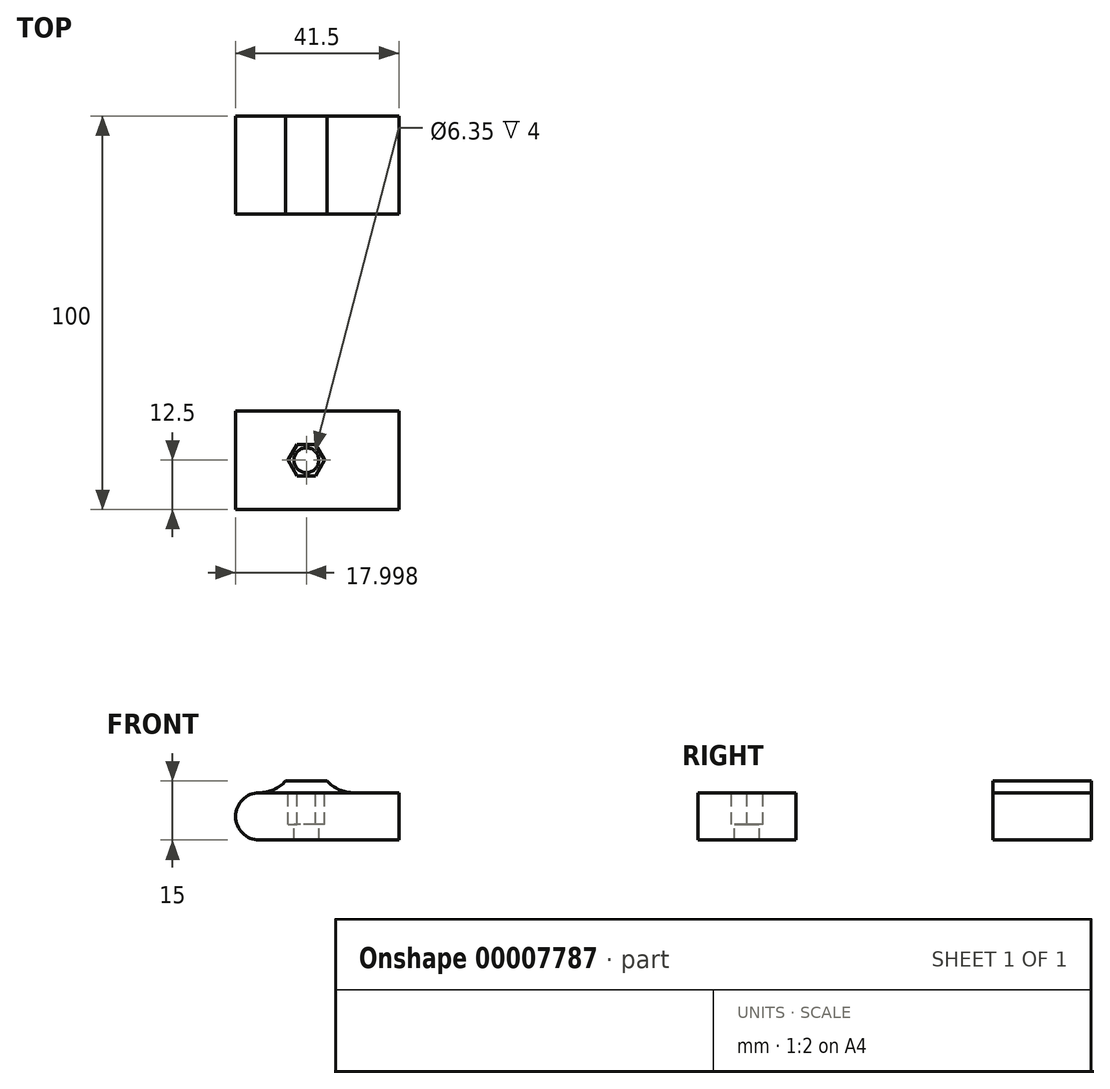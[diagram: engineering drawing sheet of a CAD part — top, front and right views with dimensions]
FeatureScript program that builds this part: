
annotation { "Feature Type Name" : "Feature", "Feature Type Description" : "" }
export const myFeature = defineFeature(function(context is Context, id is Id, definition is map)
    precondition{}
    {
        {
            var Q0;
            Q0=qCreatedBy(makeId("Front.planeOp"),FACE);
            var sketch = newSketch(context, id + "F0", { "sketchPlane" : qUnion([Q0])});
            skArc(sketch, "E0", {"start": v(-62.06, 7.13) * mm, "mid": v(-68.06, 1.13) * mm, "end": v(-62.06, -4.87) * mm});
            skLineSegment(sketch, "E1.rect.bottom", {"start": v(-44.77, 4.13) * mm, "end": v(-55.35, 4.13) * mm});
            skLineSegment(sketch, "E1.rect.top", {"start": v(-44.77, 10.13) * mm, "end": v(-55.35, 10.13) * mm});
            skLineSegment(sketch, "E1.rect.left", {"start": v(-44.77, 4.13) * mm, "end": v(-44.77, 10.13) * mm});
            skLineSegment(sketch, "E1.rect.right", {"start": v(-55.35, 4.13) * mm, "end": v(-55.35, 10.13) * mm});
            skPoint(sketch, "E1.rect.middle", {"position": v(-50.06, 7.13) * mm});
            skArc(sketch, "E2", {"start": v(-62.06, 7.13) * mm, "mid": v(-58.39, 7.92) * mm, "end": v(-55.35, 10.13) * mm});
            skLineSegment(sketch, "E3", {"start": v(-50.06, 7.13) * mm, "end": v(-50.06, 4.13) * mm, "construction": true});
            skArc(sketch, "E4.0.MirrorCS", {"start": v(-38.06, 7.13) * mm, "mid": v(-41.74, 7.92) * mm, "end": v(-44.77, 10.13) * mm});
            skLineSegment(sketch, "E5", {"start": v(-38.06, 7.13) * mm, "end": v(-26.56, 7.13) * mm});
            skLineSegment(sketch, "E6", {"start": v(-26.56, 7.13) * mm, "end": v(-26.56, -4.87) * mm});
            skLineSegment(sketch, "E7", {"start": v(-26.56, -4.87) * mm, "end": v(-62.06, -4.87) * mm});
            skSolve(sketch);
        }
        {
            var Q0;
            Q0 = qSketchRegion(id + "F0", true);
            extrude(context, id + "F1", {"entities" : qUnion([Q0]), "depth" : 25 * mm});
        }
        {
            var Q0;
            Q0=makeQuery(id+"F1.opExtrude","CAP_FACE",FACE,{"disambiguationData":[OSD([sQuery(id+"F0.wireOp",EDGE,"E0"),sQuery(id+"F0.wireOp",EDGE,"E1.rect.top"),sQuery(id+"F0.wireOp",EDGE,"E2"),sQuery(id+"F0.wireOp",EDGE,"E4.0.MirrorCS"),sQuery(id+"F0.wireOp",EDGE,"E5"),sQuery(id+"F0.wireOp",EDGE,"E6"),sQuery(id+"F0.wireOp",EDGE,"E7")])],"isStart":false});
            cPlane(context, id + "F2", {"entities" : qUnion([Q0]), "cplaneType" : CPlaneType.OFFSET, "offset" : 50 * mm, "width" : 150 * mm, "height" : 150 * mm});
        }
        {
            var Q0;
            Q0=qCreatedBy(id+"F2.planeOp",FACE);
            var sketch = newSketch(context, id + "F3", { "sketchPlane" : qUnion([Q0])});
            skArc(sketch, "E8.0", {"start": v(-62.06, 7.13) * mm, "mid": v(-68.06, 1.13) * mm, "end": v(-62.06, -4.87) * mm});
            skLineSegment(sketch, "E8.1", {"start": v(-38.06, 7.13) * mm, "end": v(-26.56, 7.13) * mm});
            skLineSegment(sketch, "E8.2", {"start": v(-26.56, 7.13) * mm, "end": v(-26.56, -4.87) * mm});
            skLineSegment(sketch, "E8.3", {"start": v(-26.56, -4.87) * mm, "end": v(-62.06, -4.87) * mm});
            skLineSegment(sketch, "E9", {"start": v(-62.06, 7.13) * mm, "end": v(-38.06, 7.13) * mm});
            skSolve(sketch);
        }
        {
            var Q0;
            Q0 = qSketchRegion(id + "F3", true);
            extrude(context, id + "F4", {"entities" : qUnion([Q0]), "depth" : 25 * mm});
        }
        {
            var Q0;
            Q0=makeQuery(id+"F4.opExtrude","SWEPT_FACE",FACE,{"disambiguationData":[OSD([sQuery(id+"F3.wireOp",EDGE,"E8.1"),sQuery(id+"F3.wireOp",EDGE,"E9")])]});
            var sketch = newSketch(context, id + "F5", { "sketchPlane" : qUnion([Q0])});
            skLineSegment(sketch, "E10", {"start": v(-50.06, -100) * mm, "end": v(-50.06, -25) * mm, "construction": true});
            skLineSegment(sketch, "E11", {"start": v(-26.56, -87.5) * mm, "end": v(-50.06, -87.5) * mm, "construction": true});
            skCircle(sketch, "E12.cCircle", {"center": v(-50.06, -87.5) * mm, "radius": 4 * mm, "construction": true});
            skLineSegment(sketch, "E12.0", {"start": v(-47.75, -91.5) * mm, "end": v(-52.37, -91.5) * mm});
            skLineSegment(sketch, "E12.1", {"start": v(-52.37, -91.5) * mm, "end": v(-54.68, -87.5) * mm});
            skLineSegment(sketch, "E12.2", {"start": v(-54.68, -87.5) * mm, "end": v(-52.37, -83.5) * mm});
            skLineSegment(sketch, "E12.3", {"start": v(-52.37, -83.5) * mm, "end": v(-47.75, -83.5) * mm});
            skLineSegment(sketch, "E12.4", {"start": v(-47.75, -83.5) * mm, "end": v(-45.44, -87.5) * mm});
            skLineSegment(sketch, "E12.5", {"start": v(-45.44, -87.5) * mm, "end": v(-47.75, -91.5) * mm});
            skPoint(sketch, "E12.0.midPoint", {"position": v(-50.06, -91.5) * mm});
            skSolve(sketch);
        }
        {
            var Q0;
            Q0 = qSketchRegion(id + "F5", true);
            extrude(context, id + "F6", {"entities" : qUnion([Q0]), "operationType" : NewBodyOperationType.REMOVE, "oppositeDirection" : true, "depth" : 8 * mm});
        }
        {
            var Q0;
            Q0=makeQuery(id+"F6.boolean.opBoolean","COPY",FACE,{"derivedFrom":makeQuery(id+"F6.opExtrude","CAP_FACE",FACE,{"disambiguationData":[OSD([sQuery(id+"F5.wireOp",EDGE,"E12.0"),sQuery(id+"F5.wireOp",EDGE,"E12.1"),sQuery(id+"F5.wireOp",EDGE,"E12.2"),sQuery(id+"F5.wireOp",EDGE,"E12.3"),sQuery(id+"F5.wireOp",EDGE,"E12.4"),sQuery(id+"F5.wireOp",EDGE,"E12.5")])],"isStart":false})});
            var sketch = newSketch(context, id + "F7", { "sketchPlane" : qUnion([Q0])});
            skCircle(sketch, "E13", {"center": v(-50.06, -87.5) * mm, "radius": 3.18 * mm});
            skLineSegment(sketch, "E14", {"start": v(-50.06, -87.5) * mm, "end": v(-50.06, -83.5) * mm, "construction": true});
            skSolve(sketch);
        }
        {
            var Q0;
            Q0 = qSketchRegion(id + "F7", true);
            extrude(context, id + "F8", {"entities" : qUnion([Q0]), "operationType" : NewBodyOperationType.REMOVE, "oppositeDirection" : true, "depth" : 25 * mm});
        }
    });
